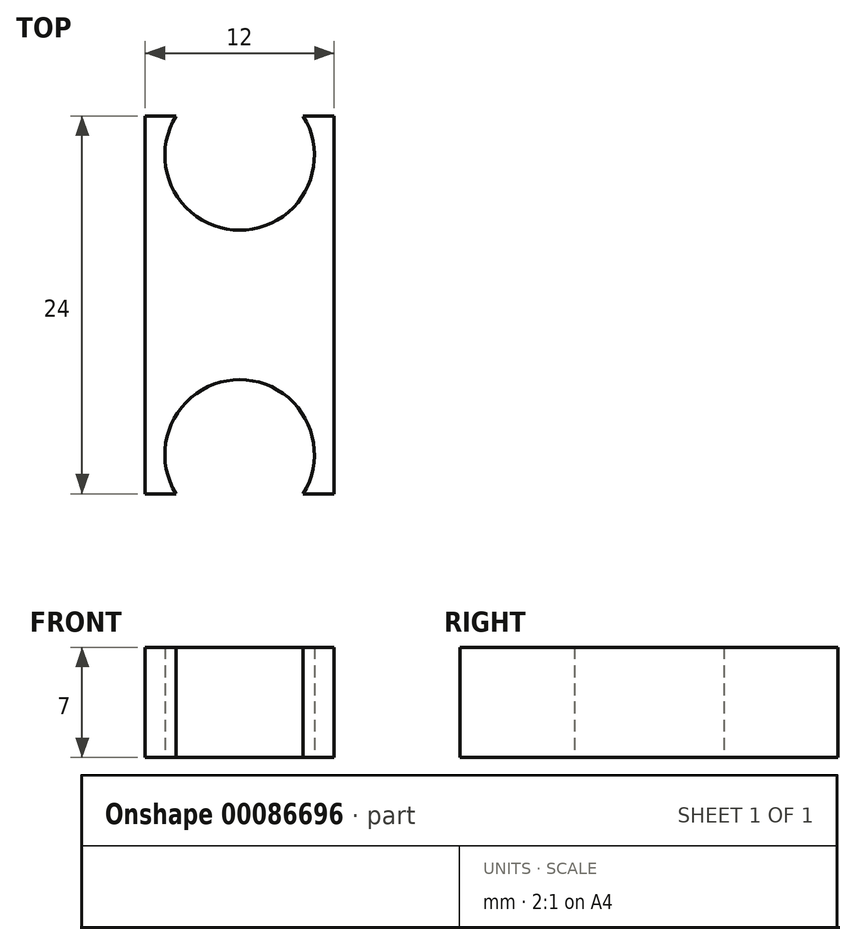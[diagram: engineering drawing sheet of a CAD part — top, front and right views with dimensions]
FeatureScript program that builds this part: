
annotation { "Feature Type Name" : "Feature", "Feature Type Description" : "" }
export const myFeature = defineFeature(function(context is Context, id is Id, definition is map)
    precondition{}
    {
        {
            var Q0;
            Q0=qCreatedBy(makeId("Top.planeOp"),FACE);
            var sketch = newSketch(context, id + "F0", { "sketchPlane" : qUnion([Q0])});
            skLineSegment(sketch, "E0.bottom", {"start": v(6, 12) * mm, "end": v(-6, 12) * mm});
            skLineSegment(sketch, "E0.top", {"start": v(6, -12) * mm, "end": v(-6, -12) * mm});
            skLineSegment(sketch, "E0.left", {"start": v(6, 12) * mm, "end": v(6, -12) * mm});
            skLineSegment(sketch, "E0.right", {"start": v(-6, 12) * mm, "end": v(-6, -12) * mm});
            skPoint(sketch, "E0.middle", {"position": v(0, 0) * mm});
            skCircle(sketch, "E1", {"center": v(0, 9.5) * mm, "radius": 4.75 * mm});
            skLineSegment(sketch, "E2", {"start": v(-15.84, 0) * mm, "end": v(20.57, 0) * mm, "construction": true});
            skPoint(sketch, "E2.endSnap0", {"position": v(6, 0) * mm});
            skCircle(sketch, "E3", {"center": v(0, -9.5) * mm, "radius": 4.75 * mm});
            skSolve(sketch);
        }
        {
            var Q0;
            {var subQ4=sQuery(id+"F0.wireOp",EDGE,"E0.left");Q0=makeQuery(id+"F0.imprint","IMPRINT",FACE,{"disambiguationData":[TD([[makeQuery(id+"F0.imprint","IMPRINT",EDGE,{"derivedFrom":subQ4}),-1.0]])]});}
            extrude(context, id + "F1", {"entities" : qUnion([Q0]), "depth" : 7 * mm});
        }
    });
